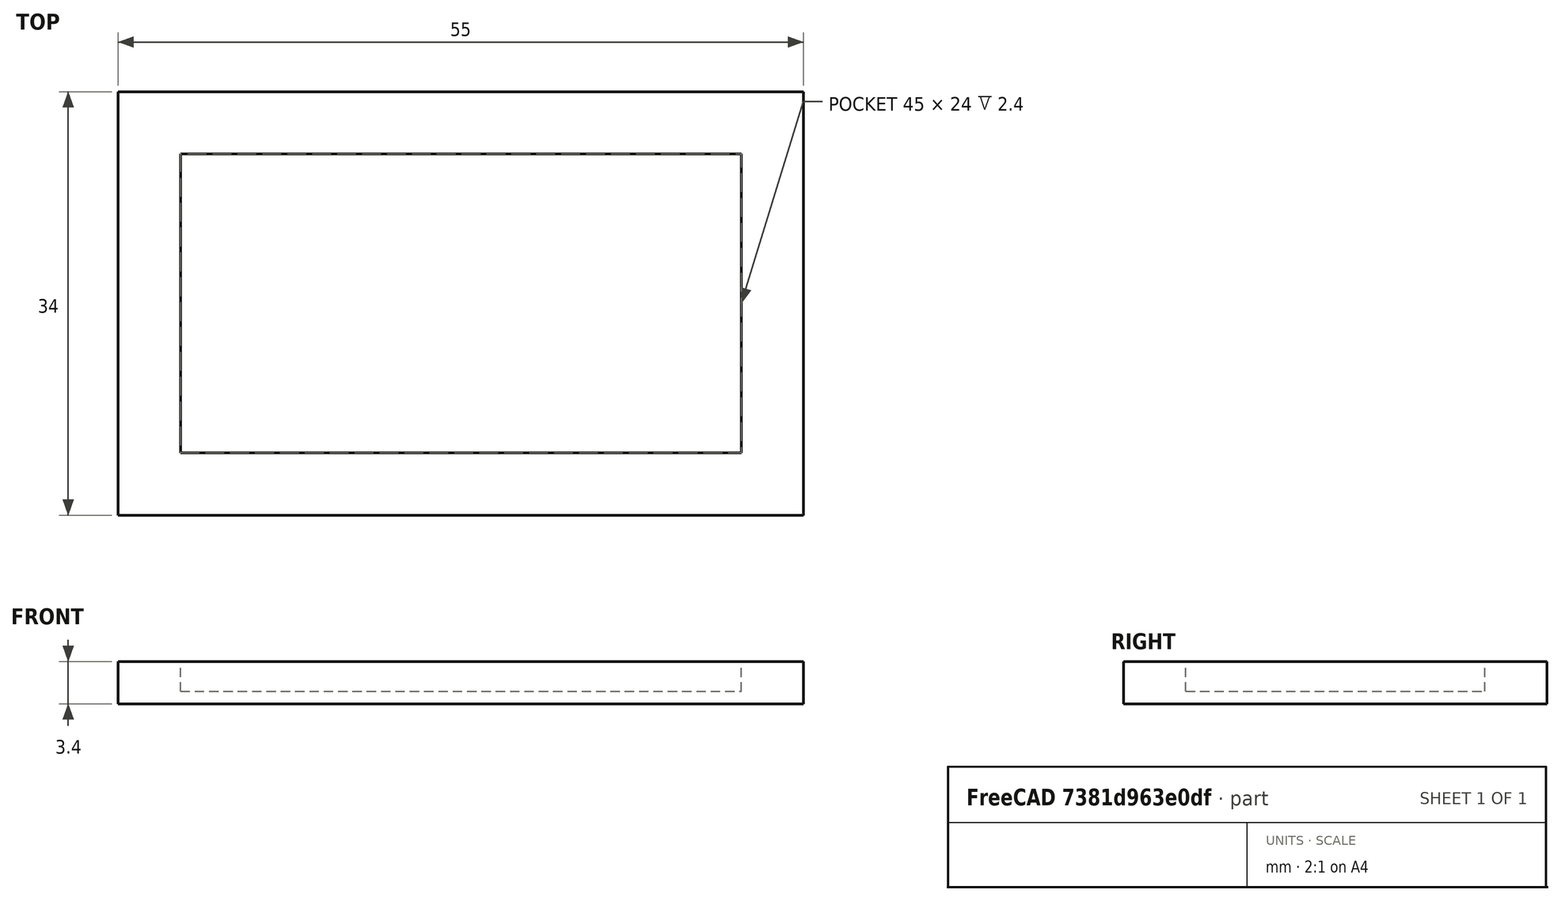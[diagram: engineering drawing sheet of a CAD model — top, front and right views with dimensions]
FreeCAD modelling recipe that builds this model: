
FCSTD DOCUMENT  (FreeCAD 0.18.4R)
Label: magnit_bottom_box
License: FreeArt
LicenseURL: http://artlibre.org/licence/lal
objects: Part::Box×2, Spreadsheet::Sheet×1, Part::Cut×1
note: 3 computed .brp shape members not serialized (recipe doc carries the construction recipe); baked Part::Feature solids carry a one-line shape summary decoded from their .brp

FEATURE [Part::Box] Box  label="bottom cube"
  AttacherType = Attacher::AttachEngine3D
  Height = 3.4
  Length = 55
  Width = 34
  expr: Height = p.bottom_wall + p.magnit_z
  expr: Width = p.box_y
  expr: Length = p.box_x
FEATURE [Spreadsheet::Sheet] Spreadsheet  label="p"
  cells = A1=magnit_x; B1(magnit_x)=45; A2=magnit_y; B2(magnit_y)=24; A3=magnit_z; B3(magnit_z)=2.4; A4=box_x; B4(box_x)=55; A5=box_y; B5(box_y)=34; A6=bottom_wall; B6(bottom_wall)=1
FEATURE [Part::Box] Box001  label="extraction cube"
  AttacherType = Attacher::AttachEngine3D
  Height = 2.4
  Length = 45
  Placement = pos=(5,5,1) rot=(0,0,1;0rad)
  Width = 24
  expr: Placement.Base.x = (p.box_x - p.magnit_x) / 2
  expr: Placement.Base.y = (p.box_y - p.magnit_y) / 2
  expr: Placement.Base.z = p.bottom_wall
  expr: Height = p.magnit_z
  expr: Width = p.magnit_y
  expr: Length = p.magnit_x
FEATURE [Part::Cut] Cut  label="magnit box cut"
  Base = -> Box
  Tool = -> Box001
